# Revit family: 44417_HOST_FACE
name_source: partatom
category: Lighting Fixtures
units: mm (PartAtom-declared; Revit-internal decimal feet)

## family parameters
Cut with Voids When Loaded = Yes
Host = Face
Light Source = Yes
Part Type = Normal
Room Calculation Point = No
Round Connector Dimension = Use Diameter
Shared = No

## types (26) — shared parameters
Color Filter = 16777215
Dimming Lamp Color Temperature Shift = <None>
Manufacturer = BEGA-US
Telephone = 805.684.0533
URL = www.bega-us.com

## per-type parameters (varying)
| type | Default Elevation | Description | Lamp | Model | Photometric Web File | Tilt Angle |
| Wall Luminaires - Directed Light | 6' - 0" | Surface wall with cutoff optics | 17.6W LED | 2260LED | 44417.ies | 90.00° |
| Wall Luminaires - Linear | 6' - 0" | Suface wall - linear with white acrylic diffuser | (1) 39W CF twin-4-p | 4425P | generic | 90.00° |
| Ceiling and Wall Luminaires - Unshielded | 0' - 0" | LED ceiling and wall luminaires - impact resistant | W LED | 33 508 | 33508.ies | 0.00° |
| Recessed Luminaires - Round | 0' - 0" | LED ceiling and wall luminaires - impact resistant | W LED | 33 508 | 33508.ies | 0.00° |
| Recessed Luminaires - Square | 0' - 0" |  | W LED |  | 88754.IES | 0.00° |
| Recessed Luminaires - Retangular | 0' - 0" | LED ceiling and wall luminaires - impact resistant | W LED | 33 508 | 33508.ies | 0.00° |
| Recessed Luminaires - Elongated | 0' - 0" | LED ceiling and wall luminaires - impact resistant | W LED | 33 508 | 33508.ies | 0.00° |
| Recessed Ceiling Luminaires - Downlights | 0' - 0" | LED ceiling and wall luminaires - impact resistant | W LED | 33 508 | 33508.ies | 0.00° |
| Recessed Ceiling Luminaires - Asymmetric | 0' - 0" | LED ceiling and wall luminaires - impact resistant | W LED | 33 508 | 33508.ies | 0.00° |
| Pendant and Cable Suspended Luminaires - Shielded | 0' - 0" | LED ceiling and wall luminaires - impact resistant | W LED | 33 508 | 33508.ies | 0.00° |
| Pendant and Cable Suspended Luminaires - Directed | 0' - 0" | LED ceiling and wall luminaires - impact resistant | W LED | 33 508 | 33508.ies | 0.00° |
| Ceiling Luminaires - Downlights | 0' - 0" | LED ceiling and wall luminaires - impact resistant | W LED | 33 508 | 33508.ies | 0.00° |
| Ceiling Luminaires - Asymmetric | 0' - 0" | LED ceiling and wall luminaires - impact resistant | W LED | 33 508 | 33508.ies | 0.00° |
| Ceiling and Wall Luminaires - Stainless Steel | 0' - 0" | LED ceiling and wall luminaires - impact resistant | W LED | 33 508 | 33508.ies | 0.00° |
| Wall Luminaires - Stainless Steel | 0' - 0" | LED ceiling and wall luminaires - impact resistant | W LED | 33 508 | 33508.ies | 0.00° |
| Wall Luminaires - Unshielded Light | 0' - 0" | LED ceiling and wall luminaires - impact resistant | W LED | 33 508 | 33508.ies | 0.00° |
| Wall Luminaires - Shielded Light | 0' - 0" | LED ceiling and wall luminaires - impact resistant | W LED | 33 508 | 33508.ies | 0.00° |
| On-Ground Luminaires | 0' - 0" | LED ceiling and wall luminaires - impact resistant | W LED | 33 508 | 33508.ies | 0.00° |
| Light Design Elements | 0' - 0" | LED ceiling and wall luminaires - impact resistant | W LED | 33 508 | 33508.ies | 0.00° |
| LED System Bollard | 0' - 0" | LED ceiling and wall luminaires - impact resistant | W LED | 33 508 | 33508.ies | 0.00° |
| Bollards | 0' - 0" | LED ceiling and wall luminaires - impact resistant | W LED | 33 508 | 33508.ies | 0.00° |
| Bollards - Stainless Steel | 0' - 0" | LED ceiling and wall luminaires - impact resistant | W LED | 33 508 | 33508.ies | 0.00° |
| Light Building Elements | 0' - 0" | LED ceiling and wall luminaires - impact resistant | W LED | 33 508 | 33508.ies | 0.00° |
| Pole-top Luminaires - with asymmetrical light distribution | 0' - 0" | LED ceiling and wall luminaires - impact resistant | W LED | 33 508 | 33508.ies | 0.00° |
| Pole-top Luminaires - with symmetrical light distribution | 0' - 0" | LED ceiling and wall luminaires - impact resistant | W LED | 33 508 | 33508.ies | 0.00° |
| Pole-top Luminaires - with indirect light | 0' - 0" | LED ceiling and wall luminaires - impact resistant | W LED | 33 508 | 88754.IES | 0.00° |

## geometry (parser evidence)
native form markers: Blend x19, Sweep x16
no freeform markers — native parametric forms only
